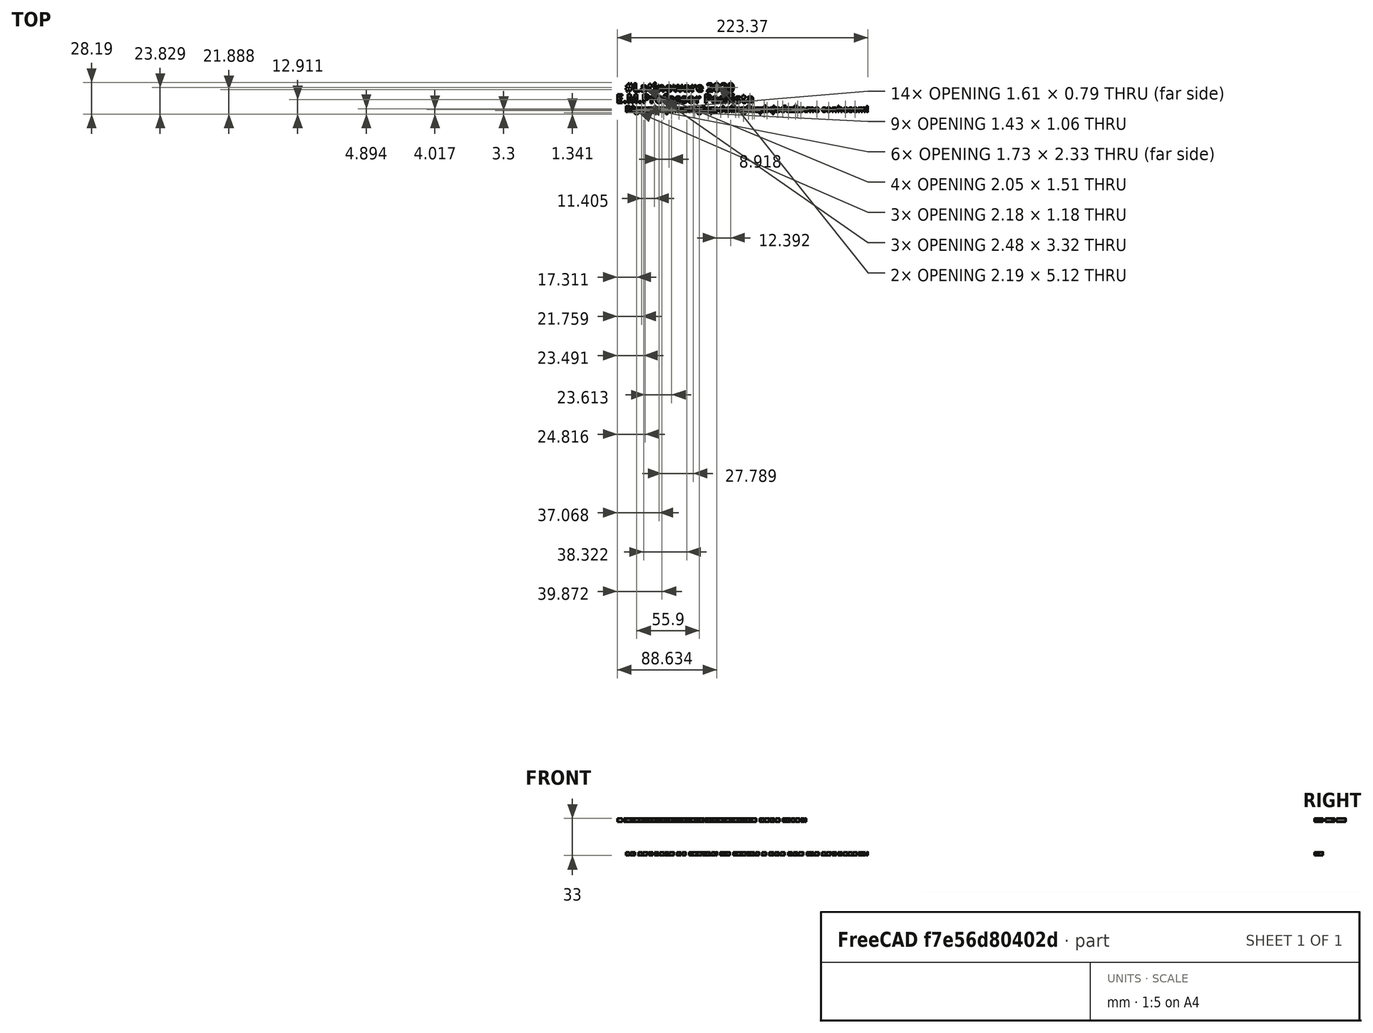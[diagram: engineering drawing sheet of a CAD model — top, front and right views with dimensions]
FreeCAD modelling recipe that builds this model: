
FCSTD DOCUMENT  (FreeCAD 0.19R)
Label: DUVIDO-01
License: Creative Commons Attribution-NonCommercial
LicenseURL: http://creativecommons.org/licenses/by-nc/4.0/
objects: Part::Part2DObjectPython×4, Part::Extrusion×4
note: 8 computed .brp shape members not serialized (recipe doc carries the construction recipe); baked Part::Feature solids carry a one-line shape summary decoded from their .brp

FEATURE [Part::Part2DObjectPython] ShapeString  # Draft 2D object (typed FeaturePython)
  FontFile = <path>
  Size = 10
  String = E.M.Professor Paulista
  Tracking = 0
FEATURE [Part::Part2DObjectPython] ShapeString001  # Draft 2D object (typed FeaturePython)
  FontFile = <path>
  Placement = pos=(8,10,0) rot=(0,0,1;0rad)
  Size = 10
  String = #Latinoware 2020
  Tracking = 0
FEATURE [Part::Extrusion] Extrude
  Base = -> ShapeString
  Dir = (0,0,1)
  DirMode = 2
  FaceMakerClass = Part::FaceMakerBullseye
  LengthFwd = 3
  LengthRev = 0
  Solid = false
  Symmetric = false
FEATURE [Part::Extrusion] Extrude001
  Base = -> ShapeString001
  Dir = (0,0,1)
  DirMode = 2
  FaceMakerClass = Part::FaceMakerBullseye
  LengthFwd = 3
  LengthRev = 0
  Solid = false
  Symmetric = false
FEATURE [Part::Part2DObjectPython] ShapeString002  # Draft 2D object (typed FeaturePython)
  FontFile = <path>
  Placement = pos=(8,-8,0) rot=(0,0,1;0rad)
  Size = 7
  String = Diga para um nerd que ele não pode fazer.
  Tracking = 0
FEATURE [Part::Extrusion] Extrude002
  Base = -> ShapeString002
  Dir = (0,0,1)
  DirMode = 2
  FaceMakerClass = Part::FaceMakerBullseye
  LengthFwd = 3
  LengthRev = 0
  Solid = false
  Symmetric = false
FEATURE [Part::Part2DObjectPython] ShapeString003  # Draft 2D object (typed FeaturePython)
  FontFile = <path>
  Placement = pos=(8,-8,-30) rot=(0,0,1;0rad)
  Size = 7
  String = Eu conheço as regras. As regras é que não me conhecem!
  Tracking = 0
FEATURE [Part::Extrusion] Extrude003
  Base = -> ShapeString003
  Dir = (0,0,1)
  DirMode = 2
  FaceMakerClass = Part::FaceMakerBullseye
  LengthFwd = 3
  LengthRev = 0
  Solid = false
  Symmetric = false
note: 4 file-system paths scrubbed to <path> (originals preserved in the JSON sidecar)
